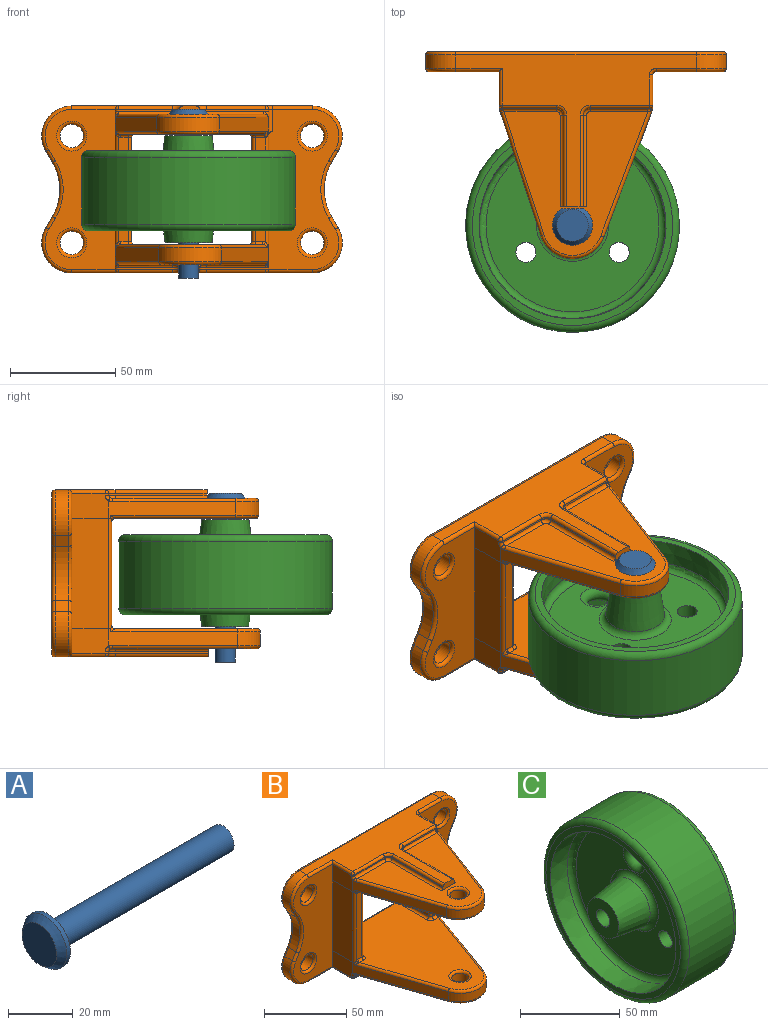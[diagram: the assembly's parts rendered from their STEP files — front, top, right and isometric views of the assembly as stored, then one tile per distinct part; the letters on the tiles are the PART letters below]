
ASSEMBLY  parts=3 mates=2
PART A: 7 faces, bbox 80.3x19.1x19.1 mm
  f0: plane 19.05x17.46mm, normal (1,0,0), area 202.4mm2, adj f1,f5,f6
  f1: cylinder r=4.76mm len=76.2mm, axis (-1,0,0), area 2280.2mm2, adj f0,f2
  f2: plane 9.53x9.53mm, normal (1,0,0), area 71.3mm2, adj f1
  f3: plane 15.14x15.14mm, normal (-1,0,0), area 180mm2, adj f4
  f4: cone r=9.53mm half-angle=38deg, axis (1,0,0), area 152.1mm2, adj f3,f5,f6
  f5: cylinder r=9.53mm len=19.05mm, axis (-1,0,0), area 77.3mm2, adj f0,f4,f6
  f6: plane 10.54x3.62mm, normal (0,1,0), area 30.7mm2, adj f0,f4,f5
PART B: 193 faces, bbox 145.7x101x82.2 mm
  f0: plane 17.49x0.01mm, normal (0,0,1), area 0.2mm2, adj f20,f80,f84,f92,f118
  f1: plane 95.25x67.41mm, normal (0,0,-1), area 4287.1mm2, adj f121,f122,f123,f158,f159,f160,f165,f166
  f2: plane 96.03x67.44mm, normal (0,0,1), area 4324.5mm2, adj f149,f150,f151,f163,f171,f172,f173,f178
  f3: plane 17.49x0.01mm, normal (0,0,-1), area 0.2mm2, adj f11,f73,f77,f88,f119
  f4: plane 28.2x0.79mm, normal (0,-1,0), area 22.4mm2, adj f9,f133,f137,f143
  f5: plane 44.43x0.79mm, normal (1,0,0), area 35.3mm2, adj f6,f9,f136,f145
  f6: plane 12.7x3.97mm, normal (0,-1,0), area 37.8mm2, adj f5,f7,f24,f85,f136,f140,f145,f146
  f7: plane 44.43x0.79mm, normal (-1,0,0), area 35.3mm2, adj f6,f10,f140,f146
  f8: plane 25.77x0.79mm, normal (0,-1,0), area 20.5mm2, adj f10,f139,f148,f191
  f9: cylinder r=3.17mm len=3.18mm, axis (0,0,-1), area 4mm2, adj f4,f5,f138,f144
  f10: cylinder r=3.17mm len=3.18mm, axis (0,0,-1), area 4mm2, adj f7,f8,f141,f147
  f11: plane 76.2x33.35mm, normal (0,-1,0), area 1906.5mm2, adj f3,f12,f22,f56,f57,f63,f65,f67
  f12: cylinder r=1.59mm len=22.23mm, axis (-1,0,0), area 53.4mm2, adj f11,f24,f70,f190
  f13: plane 25.73x0.79mm, normal (0,-1,0), area 20.4mm2, adj f18,f100,f104,f107
  f14: plane 43.66x0.79mm, normal (-1,0,0), area 34.7mm2, adj f15,f18,f96,f109
  f15: plane 12.7x3.97mm, normal (0,-1,0), area 37.8mm2, adj f14,f16,f30,f78,f96,f109,f110,f113
  f16: plane 43.66x0.79mm, normal (1,0,0), area 34.7mm2, adj f15,f19,f110,f113
  f17: plane 28.24x0.87mm, normal (0,-1,0), area 22.4mm2, adj f19,f112,f115,f116,f130
  f18: cylinder r=3.17mm len=3.18mm, axis (0,0,1), area 4mm2, adj f13,f14,f97,f108
  f19: cylinder r=3.17mm len=3.18mm, axis (0,0,1), area 4mm2, adj f16,f17,f111,f114
  f20: plane 76.2x33.35mm, normal (0,-1,0), area 1889.4mm2, adj f0,f21,f58,f59,f60,f61,f62,f64
  f21: cylinder r=1.59mm len=19.05mm, axis (1,0,0), area 47.5mm2, adj f20,f30,f61,f127
  f22: plane 17.49x0.01mm, normal (0,0,1), area 0.2mm2, adj f11,f79,f82,f88,f119
  f23: cylinder r=14.29mm len=21.55mm, axis (0,1,0), area 190.9mm2, adj f24,f34,f41,f70
  f24: plane 114.3x73.01mm, normal (0,0,-1), area 2267.7mm2, adj f6,f12,f23,f25,f40,f68,f134,f136
  f25: cylinder r=14.29mm len=21.55mm, axis (0,1,0), area 190.9mm2, adj f24,f26,f42,f66
  f26: plane 6.35x5.24mm, normal (0.86,0,0.51), area 38.6mm2, adj f25,f27,f44,f64
  f27: cylinder r=25.4mm len=25.8mm, axis (0,1,0), area 171.9mm2, adj f26,f28,f46,f62
  f28: plane 6.35x5.24mm, normal (0.86,0,-0.51), area 38.6mm2, adj f27,f29,f48,f60
  f29: cylinder r=14.29mm len=21.55mm, axis (0,1,0), area 190.9mm2, adj f28,f30,f50,f61
  f30: plane 114.3x72.23mm, normal (0,0,1), area 2264.9mm2, adj f15,f21,f29,f31,f51,f63,f96,f97
  f31: cylinder r=14.29mm len=21.55mm, axis (0,1,0), area 190.9mm2, adj f30,f32,f49,f65
  f32: plane 6.35x5.24mm, normal (-0.86,0,-0.51), area 38.6mm2, adj f31,f33,f47,f67
  f33: cylinder r=25.4mm len=25.8mm, axis (0,1,0), area 171.9mm2, adj f32,f34,f45,f69
  f34: plane 6.35x5.24mm, normal (-0.86,0,0.51), area 38.6mm2, adj f23,f33,f43,f71
  f35: cylinder r=5.56mm len=11.11mm, axis (0,1,0), area 221.7mm2, adj f55,f59
  f36: cylinder r=5.56mm len=11.11mm, axis (0,1,0), area 221.7mm2, adj f54,f58
  f37: cylinder r=5.56mm len=11.11mm, axis (0,1,0), area 221.7mm2, adj f53,f57
  f38: cylinder r=5.56mm len=11.11mm, axis (0,1,0), area 221.7mm2, adj f52,f56
  f39: plane 139.7x76.2mm, normal (0,1,0), area 6033.5mm2, adj f40,f41,f42,f43,f44,f45,f46,f47
  f40: cylinder r=1.59mm len=114.3mm, axis (1,0,0), area 285mm2, adj f24,f39,f41,f42
  f41: torus R=12.7mm, axis (0,-1,0), area 71.9mm2, adj f23,f39,f40,f43
  f42: torus R=12.7mm, axis (0,-1,0), area 71.9mm2, adj f25,f39,f40,f44
  f43: cylinder r=1.59mm len=6.05mm, axis (-0.51,0,-0.86), area 15.2mm2, adj f34,f39,f41,f45
  f44: cylinder r=1.59mm len=6.05mm, axis (-0.51,0,0.86), area 15.2mm2, adj f26,f39,f42,f46
  f45: torus R=26.99mm, axis (0,-1,0), area 69mm2, adj f33,f39,f43,f47
  f46: torus R=26.99mm, axis (0,-1,0), area 69mm2, adj f27,f39,f44,f48
  f47: cylinder r=1.59mm len=6.05mm, axis (0.51,0,-0.86), area 15.2mm2, adj f32,f39,f45,f49
  f48: cylinder r=1.59mm len=6.05mm, axis (0.51,0,0.86), area 15.2mm2, adj f28,f39,f46,f50
  f49: torus R=12.7mm, axis (0,-1,0), area 71.9mm2, adj f31,f39,f47,f51
  f50: torus R=12.7mm, axis (0,-1,0), area 71.9mm2, adj f29,f39,f48,f51
  f51: cylinder r=1.59mm len=114.3mm, axis (-1,0,0), area 285mm2, adj f30,f39,f49,f50
  f52: torus R=7.14mm, axis (0,-1,0), area 96.1mm2, adj f38,f39
  f53: torus R=7.14mm, axis (0,-1,0), area 96.1mm2, adj f37,f39
  f54: torus R=7.14mm, axis (0,-1,0), area 96.1mm2, adj f36,f39
  f55: torus R=7.14mm, axis (0,-1,0), area 96.1mm2, adj f35,f39
  f56: torus R=7.14mm, axis (0,-1,0), area 96.1mm2, adj f11,f38
  f57: torus R=7.14mm, axis (0,-1,0), area 96.1mm2, adj f11,f37
  f58: torus R=7.14mm, axis (0,-1,0), area 96.1mm2, adj f20,f36
  f59: torus R=7.14mm, axis (0,-1,0), area 96.1mm2, adj f20,f35
  f60: cylinder r=1.59mm len=6.05mm, axis (-0.51,0,-0.86), area 15.2mm2, adj f20,f28,f61,f62
  f61: torus R=12.7mm, axis (0,-1,0), area 71.9mm2, adj f20,f21,f29,f60
  f62: torus R=26.99mm, axis (0,-1,0), area 69mm2, adj f20,f27,f60,f64
  f63: cylinder r=1.59mm len=22.23mm, axis (1,0,0), area 53.4mm2, adj f11,f30,f65,f99
  f64: cylinder r=1.59mm len=6.05mm, axis (0.51,0,-0.86), area 15.2mm2, adj f20,f26,f62,f66
  f65: torus R=12.7mm, axis (0,-1,0), area 71.9mm2, adj f11,f31,f63,f67
  f66: torus R=12.7mm, axis (0,-1,0), area 71.9mm2, adj f20,f25,f64,f68
  f67: cylinder r=1.59mm len=6.05mm, axis (-0.51,0,0.86), area 15.2mm2, adj f11,f32,f65,f69
  f68: cylinder r=1.59mm len=22.23mm, axis (-1,0,0), area 53.4mm2, adj f20,f24,f66,f134
  f69: torus R=26.99mm, axis (0,-1,0), area 69mm2, adj f11,f33,f67,f71
  f70: torus R=12.7mm, axis (0,-1,0), area 71.9mm2, adj f11,f12,f23,f71
  f71: cylinder r=1.59mm len=6.05mm, axis (0.51,0,0.86), area 15.2mm2, adj f11,f34,f69,f70
  f72: plane 15.88x11.91mm, normal (1,0,0), area 183.8mm2, adj f75,f125,f126,f128,f130,f131,f132
  f73: plane 17.46x11.91mm, normal (-1,0,0), area 203.6mm2, adj f3,f11,f77,f99,f104,f106
  f74: cylinder r=15.88mm len=29.92mm, axis (0,0,1), area 248.1mm2, adj f75,f77,f101,f159
  f75: plane 61.7x23.81mm, normal (0.93,-0.36,0), area 418.2mm2, adj f72,f74,f93,f98,f116,f118,f124,f131
  f76: cylinder r=5.16mm len=10.32mm, axis (0,0,1), area 205.8mm2, adj f164,f165
  f77: plane 60.65x19.92mm, normal (-0.95,-0.31,0), area 406.2mm2, adj f3,f73,f74,f86,f103,f105,f106,f119
  f78: plane 68.53x68.26mm, normal (0,0,1), area 2272.6mm2, adj f15,f98,f101,f103,f107,f108,f109,f113
  f79: plane 17.46x11.91mm, normal (-1,0,0), area 203.6mm2, adj f11,f22,f82,f189,f190,f191
  f80: plane 17.5x11.94mm, normal (1,0,0), area 205.3mm2, adj f0,f20,f84,f133,f134,f142,f157
  f81: cylinder r=15.88mm len=29.97mm, axis (0,0,-1), area 248.9mm2, adj f82,f84,f150,f154
  f82: plane 61.56x20.8mm, normal (-0.95,-0.32,0), area 413.5mm2, adj f22,f79,f81,f87,f119,f151,f152,f153
  f83: cylinder r=5.16mm len=10.32mm, axis (0,0,-1), area 205.8mm2, adj f162,f163
  f84: plane 61.92x22.58mm, normal (0.94,-0.34,0), area 419.5mm2, adj f0,f80,f81,f91,f118,f149,f155,f156
  f85: plane 69.04x68.55mm, normal (0,0,-1), area 2300.2mm2, adj f6,f143,f144,f145,f146,f147,f148,f153
  f86: plane 0.89x0.29mm, normal (0,0,1), area 0mm2, adj f77,f119
  f87: plane 0.91x0.31mm, normal (0,0,-1), area 0mm2, adj f82,f119
  f88: plane 52.39x17.46mm, normal (-1,0,0), area 914.8mm2, adj f3,f11,f22,f119
  f89: plane 49.21x25.4mm, normal (1,0,0), area 1250mm2, adj f120,f166,f180,f183
  f90: plane 49.59x4.59mm, normal (0,-1,0), area 225.9mm2, adj f119,f120,f168,f169,f177,f178
  f91: plane 0.97x0.35mm, normal (0,0,-1), area 0.1mm2, adj f84,f118
  f92: plane 52.22x17.46mm, normal (1,0,0), area 911.9mm2, adj f0,f20,f118,f125
  f93: plane 1.02x0.39mm, normal (0,0,1), area 0.1mm2, adj f75,f118,f161
  f94: plane 49.21x25.4mm, normal (-1,0,0), area 1250mm2, adj f117,f123,f171,f186
  f95: plane 49.44x4.92mm, normal (0,-1,0), area 242.2mm2, adj f117,f118,f121,f161,f173,f174
  f96: cylinder r=1.59mm len=43.66mm, axis (0,-1,0), area 108.9mm2, adj f14,f15,f30,f97
  f97: torus R=4.76mm, axis (0,0,1), area 14.7mm2, adj f18,f30,f96,f100
  f98: cylinder r=1.59mm len=60.76mm, axis (0.36,0.93,0), area 159.1mm2, adj f75,f78,f101,f116
  f99: cylinder r=1.59mm len=17.46mm, axis (0,-1,0), area 41.6mm2, adj f30,f63,f73,f102
  f100: cylinder r=1.59mm len=25.73mm, axis (1,0,0), area 64.2mm2, adj f13,f30,f97,f102
  f101: torus R=14.29mm, axis (0,0,1), area 93.9mm2, adj f74,f78,f98,f103
  f102: sphere r=1.59mm, area 4mm2, adj f99,f100,f104
  f103: cylinder r=1.59mm len=58.91mm, axis (0.31,-0.95,0), area 153.2mm2, adj f77,f78,f101,f105
  f104: cylinder r=1.59mm len=1.59mm, axis (0,0,1), area 2mm2, adj f13,f73,f102,f106
  f105: bspline ~2.17x2.01mm, area 3.7mm2, adj f77,f103,f106,f107
  f106: torus R=3.17mm, axis (-1,0,0), area 5.5mm2, adj f73,f77,f104,f105,f107
  f107: cylinder r=1.59mm len=25.73mm, axis (-1,0,0), area 63.9mm2, adj f13,f78,f105,f106,f108
  f108: torus R=1.59mm, axis (0,0,1), area 10.2mm2, adj f18,f78,f107,f109
  f109: cylinder r=1.59mm len=43.66mm, axis (0,1,0), area 108.9mm2, adj f14,f15,f78,f108
  f110: cylinder r=1.59mm len=43.66mm, axis (0,1,0), area 108.9mm2, adj f15,f16,f30,f111
  f111: torus R=4.76mm, axis (0,0,1), area 14.7mm2, adj f19,f30,f110,f112
  f112: cylinder r=1.59mm len=28.24mm, axis (1,0,0), area 70.4mm2, adj f17,f30,f111,f129
  f113: cylinder r=1.59mm len=43.66mm, axis (0,-1,0), area 108.9mm2, adj f15,f16,f78,f114
  f114: torus R=1.59mm, axis (0,0,1), area 10.2mm2, adj f19,f78,f113,f115
  f115: cylinder r=1.59mm len=27.52mm, axis (-1,0,0), area 68.6mm2, adj f17,f78,f114,f116
  f116: bspline ~3.79x3.4mm, area 3.4mm2, adj f17,f75,f98,f115,f132
  f117: cylinder r=1.59mm len=49.21mm, axis (0,0,1), area 122.7mm2, adj f94,f95,f122,f172
  f118: cylinder r=1.59mm len=53.24mm, axis (0,0,-1), area 128.6mm2, adj f0,f75,f84,f91,f92,f93,f95,f124
  f119: cylinder r=1.59mm len=54.21mm, axis (0,0,1), area 129.2mm2, adj f3,f22,f77,f82,f86,f87,f88,f90
  f120: cylinder r=1.59mm len=49.21mm, axis (0,0,-1), area 122.7mm2, adj f89,f90,f167,f179
  f121: cylinder r=1.59mm len=4.82mm, axis (-1,0,0), area 10.5mm2, adj f1,f95,f122,f161
  f122: torus R=3.17mm, axis (0,0,1), area 8.5mm2, adj f1,f117,f121,f123
  f123: cylinder r=1.59mm len=25.4mm, axis (0,-1,0), area 63.3mm2, adj f1,f94,f122,f188
  f124: bspline ~0.18x0.1mm, area 0mm2, adj f75,f118,f125
  f125: cylinder r=1.59mm len=17.46mm, axis (0,-1,0), area 4.2mm2, adj f20,f72,f92,f124,f126
  f126: cylinder r=1.59mm len=11.91mm, axis (0,0,-1), area 27.9mm2, adj f20,f72,f125,f127
  f127: torus R=3.17mm, axis (0,0,1), area 8.5mm2, adj f21,f30,f126,f128
  f128: cylinder r=1.59mm len=14.29mm, axis (0,1,0), area 35.6mm2, adj f30,f72,f127,f129
  f129: sphere r=1.59mm, area 4mm2, adj f112,f128,f130
  f130: cylinder r=1.59mm len=1.59mm, axis (0,0,-1), area 2.2mm2, adj f17,f72,f129,f132
  f131: bspline ~2.52x1.17mm, area 0.7mm2, adj f72,f75,f132
  f132: bspline ~4.36x2.33mm, area 6.3mm2, adj f72,f116,f130,f131
  f133: cylinder r=1.59mm len=1.59mm, axis (0,0,-1), area 2mm2, adj f4,f80,f135,f142
  f134: cylinder r=1.59mm len=17.46mm, axis (0,1,0), area 41.6mm2, adj f24,f68,f80,f135
  f135: sphere r=1.59mm, area 4mm2, adj f133,f134,f137
  f136: cylinder r=1.59mm len=44.43mm, axis (0,1,0), area 110.8mm2, adj f5,f6,f24,f138
  f137: cylinder r=1.59mm len=28.2mm, axis (1,0,0), area 70.3mm2, adj f4,f24,f135,f138
  f138: torus R=4.76mm, axis (0,0,1), area 14.7mm2, adj f9,f24,f136,f137
  f139: cylinder r=1.59mm len=25.77mm, axis (1,0,0), area 64.3mm2, adj f8,f24,f141,f192
  f140: cylinder r=1.59mm len=44.43mm, axis (0,-1,0), area 110.8mm2, adj f6,f7,f24,f141
  f141: torus R=4.76mm, axis (0,0,1), area 14.7mm2, adj f10,f24,f139,f140
  f142: torus R=3.17mm, axis (0,0,-1), area 2.5mm2, adj f80,f133,f143,f157
  f143: cylinder r=1.59mm len=28.2mm, axis (1,0,0), area 70mm2, adj f4,f85,f142,f144,f156
  f144: torus R=1.59mm, axis (0,0,-1), area 10.2mm2, adj f9,f85,f143,f145
  f145: cylinder r=1.59mm len=44.43mm, axis (0,1,0), area 110.8mm2, adj f5,f6,f85,f144
  f146: cylinder r=1.59mm len=44.43mm, axis (0,-1,0), area 110.8mm2, adj f6,f7,f85,f147
  f147: torus R=1.59mm, axis (0,0,-1), area 10.2mm2, adj f10,f85,f146,f148
  f148: cylinder r=1.59mm len=25.77mm, axis (1,0,0), area 64mm2, adj f8,f85,f147,f152,f189
  f149: cylinder r=1.59mm len=61.09mm, axis (0.34,0.94,0), area 157mm2, adj f2,f84,f150,f174,f175
  f150: torus R=14.29mm, axis (0,0,-1), area 94.2mm2, adj f2,f81,f149,f151
  f151: cylinder r=1.59mm len=60.78mm, axis (0.32,-0.95,0), area 154.9mm2, adj f2,f82,f150,f176,f177
  f152: bspline ~2.48x2.34mm, area 3.8mm2, adj f82,f148,f153,f189
  f153: cylinder r=1.59mm len=59.81mm, axis (-0.32,0.95,0), area 156mm2, adj f82,f85,f152,f154
  f154: torus R=14.29mm, axis (0,0,-1), area 94.2mm2, adj f81,f85,f153,f155
  f155: cylinder r=1.59mm len=60.17mm, axis (-0.34,-0.94,0), area 158.2mm2, adj f84,f85,f154,f156
  f156: bspline ~2.17x1.89mm, area 3.6mm2, adj f84,f143,f155,f157
  f157: bspline ~1.97x1.91mm, area 1.9mm2, adj f80,f84,f142,f156
  f158: cylinder r=1.59mm len=59.89mm, axis (-0.31,0.95,0), area 152.2mm2, adj f1,f77,f159,f169,f170
  f159: torus R=14.29mm, axis (0,0,1), area 93.9mm2, adj f1,f74,f158,f160
  f160: cylinder r=1.59mm len=58.04mm, axis (-0.36,-0.93,0), area 153.4mm2, adj f1,f75,f159,f161
  f161: bspline ~3.73x3.73mm, area 6.6mm2, adj f75,f93,f95,f118,f121,f160
  f162: torus R=6.75mm, axis (0,0,-1), area 89.9mm2, adj f83,f85
  f163: torus R=6.75mm, axis (0,0,-1), area 89.9mm2, adj f2,f83
  f164: torus R=6.75mm, axis (0,0,1), area 89.9mm2, adj f76,f78
  f165: torus R=6.75mm, axis (0,0,1), area 89.9mm2, adj f1,f76
  f166: cylinder r=1.59mm len=25.4mm, axis (0,1,0), area 63.3mm2, adj f1,f89,f167,f185
  f167: torus R=3.17mm, axis (0,0,1), area 8.5mm2, adj f1,f120,f166,f168
  f168: cylinder r=1.59mm len=3.48mm, axis (1,0,0), area 8.7mm2, adj f1,f90,f167,f169
  f169: bspline ~1.99x1.74mm, area 2mm2, adj f90,f158,f168,f170
  f170: bspline ~3.13x2.23mm, area 3.6mm2, adj f77,f119,f158,f169
  f171: cylinder r=1.59mm len=25.4mm, axis (0,-1,0), area 63.3mm2, adj f2,f94,f172,f184
  f172: torus R=3.17mm, axis (0,0,-1), area 8.5mm2, adj f2,f117,f171,f173
  f173: cylinder r=1.59mm len=3.68mm, axis (-1,0,0), area 9.2mm2, adj f2,f95,f172,f174
  f174: bspline ~2.02x1.74mm, area 2.2mm2, adj f95,f149,f173,f175
  f175: bspline ~3.14x2.14mm, area 3.5mm2, adj f84,f118,f149,f174
  f176: bspline ~3.14x2.19mm, area 3.6mm2, adj f82,f119,f151,f177
  f177: bspline ~1.68x1.59mm, area 2mm2, adj f90,f151,f176,f178
  f178: cylinder r=1.59mm len=3.44mm, axis (-1,0,0), area 8.6mm2, adj f2,f90,f177,f179
  f179: torus R=3.17mm, axis (0,0,-1), area 8.5mm2, adj f2,f120,f178,f180
  f180: cylinder r=1.59mm len=25.4mm, axis (0,1,0), area 63.3mm2, adj f2,f89,f179,f181
  f181: torus R=3.17mm, axis (0,-1,0), area 8.5mm2, adj f39,f180,f182,f183
  f182: cylinder r=1.59mm len=53.98mm, axis (-1,0,0), area 134.6mm2, adj f2,f39,f181,f184
  f183: cylinder r=1.59mm len=49.21mm, axis (0,0,1), area 122.7mm2, adj f39,f89,f181,f185
  f184: torus R=3.17mm, axis (0,-1,0), area 8.5mm2, adj f39,f171,f182,f186
  f185: torus R=3.17mm, axis (0,-1,0), area 8.5mm2, adj f39,f166,f183,f187
  f186: cylinder r=1.59mm len=49.21mm, axis (0,0,-1), area 122.7mm2, adj f39,f94,f184,f188
  f187: cylinder r=1.59mm len=53.98mm, axis (1,0,0), area 134.6mm2, adj f1,f39,f185,f188
  f188: torus R=3.17mm, axis (0,-1,0), area 8.5mm2, adj f39,f123,f186,f187
  f189: torus R=3.17mm, axis (1,0,0), area 5.5mm2, adj f79,f82,f148,f152,f191
  f190: cylinder r=1.59mm len=17.46mm, axis (0,-1,0), area 41.6mm2, adj f12,f24,f79,f192
  f191: cylinder r=1.59mm len=1.59mm, axis (0,0,-1), area 2mm2, adj f8,f79,f189,f192
  f192: sphere r=1.59mm, area 4mm2, adj f139,f190,f191
PART C: 19 faces, bbox 50.8x110x110 mm
  f0: cylinder r=50.8mm len=101.6mm, axis (-1,0,0), area 10134.1mm2, adj f12,f15
  f1: plane 95.25x95.25mm, normal (1,0,0), area 918.4mm2, adj f2,f12
  f2: cone r=44.45mm half-angle=0.1deg, axis (1,0,0), area 4678.7mm2, adj f1,f3
  f3: plane 88.86x88.86mm, normal (1,0,0), area 5213.5mm2, adj f2,f4,f16,f17,f18
  f4: cone r=14.35mm half-angle=8.1deg, axis (-1,0,0), area 1810mm2, adj f3,f5
  f5: plane 22.35x22.35mm, normal (1,0,0), area 319.2mm2, adj f4,f6
  f6: cylinder r=4.83mm len=50.8mm, axis (-1,0,0), area 1540.4mm2, adj f5,f7
  f7: plane 22.35x22.35mm, normal (-1,0,0), area 319.2mm2, adj f6,f8
  f8: cone r=11.18mm half-angle=8.2deg, axis (1,0,0), area 1546.2mm2, adj f7,f13
  f9: plane 82.22x82.22mm, normal (-1,0,0), area 4050.1mm2, adj f13,f14,f16,f17,f18
  f10: cone r=44.45mm half-angle=0.8deg, axis (-1,0,0), area 3307.3mm2, adj f11,f14
  f11: plane 95.25x95.25mm, normal (-1,0,0), area 918.4mm2, adj f10,f15
  f12: torus R=47.62mm, axis (1,0,0), area 1555.7mm2, adj f0,f1
  f13: torus R=17.1mm, axis (-1,0,0), area 432.9mm2, adj f8,f9
  f14: torus R=41.11mm, axis (-1,0,0), area 1339.3mm2, adj f9,f10
  f15: torus R=47.62mm, axis (1,0,0), area 1555.7mm2, adj f0,f11
  f16: cylinder r=4.76mm len=9.53mm, axis (-1,0,0), area 190mm2, adj f3,f9
  f17: cylinder r=4.76mm len=9.53mm, axis (-1,0,0), area 190mm2, adj f3,f9
  f18: torus R=7.94mm, axis (-1,0,0), area 370.8mm2, adj f3,f9
PLACE A rot(axis=(0,1,0),90deg) t=(-7.32,-132.7,82.17)mm
PLACE B t=(13.02,-50.15,63.03)mm
PLACE C rot(axis=(-0.58,0.58,0.58),120deg) t=(20.29,-192.47,67.68)mm
MATE fastened B.f101 <-> A.f1  axis (0,0,1) through (20.29,-132.7,104.72)mm
MATE revolute A.f1 <-> C.f0  axis (0,0,1) through (20.29,-132.7,66.62)mm
